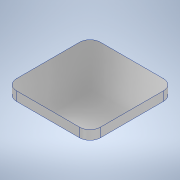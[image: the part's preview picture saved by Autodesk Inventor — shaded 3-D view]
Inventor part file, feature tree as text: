
AUTODESK INVENTOR PART (.ipt)
format: ipt  version: 2022 (Build 260153000, 153)  size: 104,960 bytes
history: native  units: in
note: dims shown in document units (in); Inventor stores cm internally (conversion verified against a paired STEP export)
features: extrude x1, fillet x1, sketch x1
ambient origin geometry x8: Origin, YZ Plane, XZ Plane, XY Plane, X Axis, Y Axis, Z Axis, Center Point
bodies: Solid1 (feature_tree)
feature tree (3):
  extrude  "Extrusion1"  Depth=0.6299in
  fillet  "Fillet1"  Radius=0.0689in
  sketch  "Sketch1"  dims[d0=0.6299in d1=0.6299in d2=0.0689in d3=0.0in d4=0.0787in]
